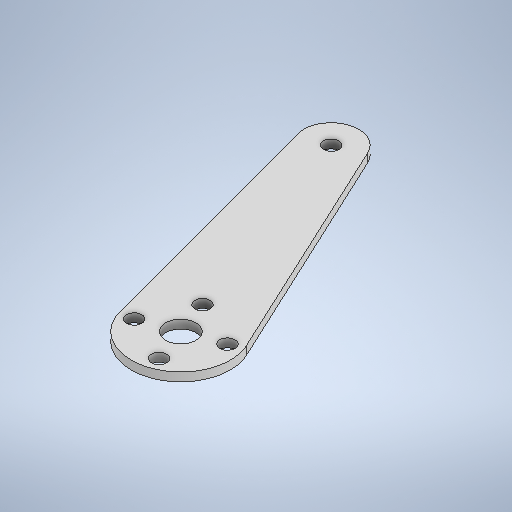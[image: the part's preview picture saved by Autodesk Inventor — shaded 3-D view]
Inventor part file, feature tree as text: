
AUTODESK INVENTOR PART (.ipt)
format: ipt  version: 2025.2 (Build 292293000, 293)  size: 291,328 bytes
history: native  units: in
note: dims shown in document units (in); Inventor stores cm internally (conversion verified against a paired STEP export)
features: extrude x3, sketch x3
ambient origin geometry x8: Origin, YZ Plane, XZ Plane, XY Plane, X Axis, Y Axis, Z Axis, Center Point
bodies: Solid1 (feature_tree)
feature tree (6):
  extrude  "Extrusion1"  Depth=0.0669in TaperAngle=0.0deg
  extrude  "Extrusion2"  Depth=0.1181in
  extrude  "Extrusion3"  Depth=0.1181in
  sketch  "Sketch1"  dims[d0=0.7731in d1=0.0669in d2=0.0in]
  sketch  "Sketch2"  dims[d3=0.2147in d4=0.1181in]
  sketch  "Sketch3"  dims[d5=0.1181in d6=0.1181in d7=0.1181in d12=0.1181in d13=0.1181in d18=1.9685in d19=0.2842in d20=0.2842in d21=0.2842in d22=0.2842in d23=0.0669in d24=0.0in d25=0.2362in d26=0.0in d27=0.0in]
